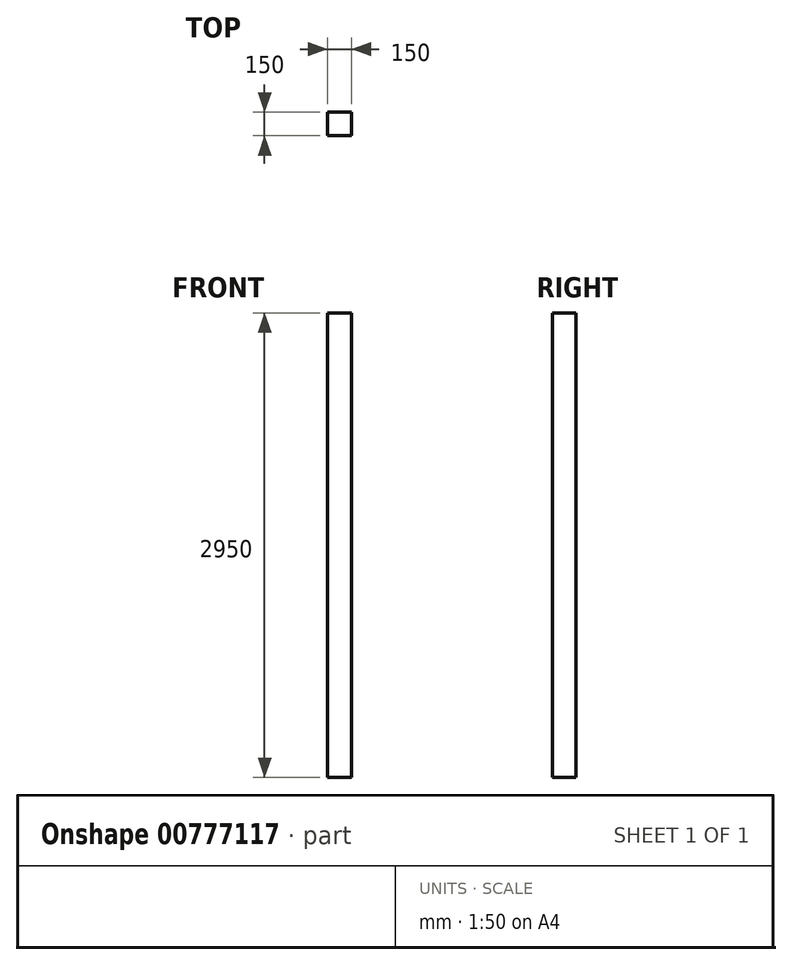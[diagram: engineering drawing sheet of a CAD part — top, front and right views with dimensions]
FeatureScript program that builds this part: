
annotation { "Feature Type Name" : "Feature", "Feature Type Description" : "" }
export const myFeature = defineFeature(function(context is Context, id is Id, definition is map)
    precondition{}
    {
        {
            var Q0;
            Q0=qCreatedBy(makeId("Top.planeOp"),FACE);
            var sketch = newSketch(context, id + "F0", { "sketchPlane" : qUnion([Q0])});
            skLineSegment(sketch, "E0.bottom", {"start": v(-75, 75) * mm, "end": v(75, 75) * mm});
            skLineSegment(sketch, "E0.top", {"start": v(-75, -75) * mm, "end": v(75, -75) * mm});
            skLineSegment(sketch, "E0.left", {"start": v(-75, 75) * mm, "end": v(-75, -75) * mm});
            skLineSegment(sketch, "E0.right", {"start": v(75, 75) * mm, "end": v(75, -75) * mm});
            skPoint(sketch, "E0.middle", {"position": v(0, 0) * mm});
            skSolve(sketch);
        }
        {
            var Q0;
            Q0=makeQuery(id+"F0.imprint","IMPRINT",FACE,{"disambiguationData":[TD([[makeQuery(id+"F0.imprint","IMPRINT",EDGE,{"derivedFrom":sQuery(id+"F0.wireOp",EDGE,"E0.bottom")}),-1.0]])]});
            extrude(context, id + "F1", {"entities" : qUnion([Q0]), "depth" : 2950 * mm, "offsetDistance" : 25 * mm});
        }
    });
